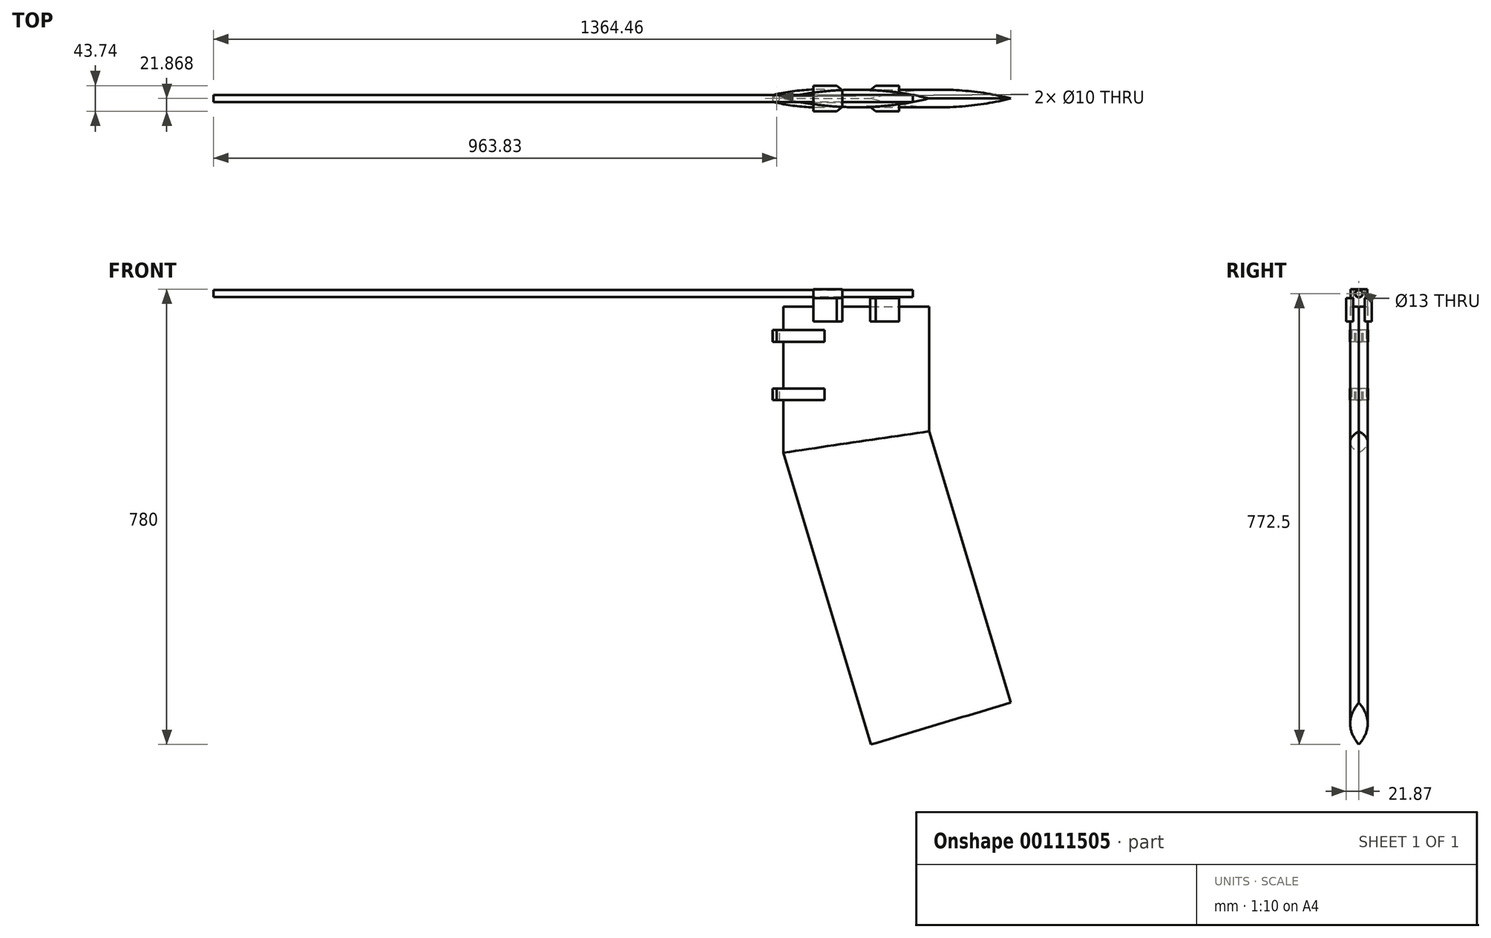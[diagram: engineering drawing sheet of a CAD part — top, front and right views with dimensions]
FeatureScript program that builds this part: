
annotation { "Feature Type Name" : "Feature", "Feature Type Description" : "" }
export const myFeature = defineFeature(function(context is Context, id is Id, definition is map)
    precondition{}
    {
        {
            var Q0;
            Q0=qCreatedBy(makeId("Front.planeOp"),FACE);
            var sketch = newSketch(context, id + "F0", { "sketchPlane" : qUnion([Q0])});
            skLineSegment(sketch, "E0.bottom", {"start": v(-150, 364.56) * mm, "end": v(100, 364.56) * mm});
            skLineSegment(sketch, "E0.top", {"start": v(0, -385.44) * mm, "end": v(250, -385.44) * mm});
            skLineSegment(sketch, "E0.left", {"start": v(-150, 364.56) * mm, "end": v(-150, 114.56) * mm});
            skLineSegment(sketch, "E1", {"start": v(100, 364.56) * mm, "end": v(100, 264.56) * mm});
            skArc(sketch, "E2", {"start": v(250, -385.44) * mm, "mid": v(188.28, -57.37) * mm, "end": v(100, 264.56) * mm});
            skLineSegment(sketch, "E3", {"start": v(250, -385.44) * mm, "end": v(0, -385.44) * mm});
            skLineSegment(sketch, "E4", {"start": v(-150, 114.56) * mm, "end": v(0, -385.44) * mm});
            skSolve(sketch);
        }
        {
            var Q0;
            Q0=sQuery(id+"F0.wireOp",EDGE,"E0.bottom");
            cPlane(context, id + "F1", {"entities" : qUnion([Q0]), "cplaneType" : CPlaneType.LINE_ANGLE, "offset" : 150 * mm, "angle" : 90 * degree, "width" : 150 * mm, "height" : 150 * mm});
        }
        {
            var Q0;
            Q0=qCreatedBy(id+"F1.planeOp",FACE);
            var sketch = newSketch(context, id + "F2", { "sketchPlane" : qUnion([Q0])});
            skLineSegment(sketch, "E5", {"start": v(-150, 0) * mm, "end": v(100, 0) * mm});
            skArc(sketch, "E6", {"start": v(100, 0) * mm, "mid": v(-25, 15) * mm, "end": v(-150, 0) * mm});
            skArc(sketch, "E7.MirrorCS", {"start": v(100, 0) * mm, "mid": v(-25, -15) * mm, "end": v(-150, 0) * mm});
            skSolve(sketch);
        }
        {
            var Q0;
            Q0=makeQuery(id+"F2.imprint","IMPRINT",FACE,{"disambiguationData":[TD([[makeQuery(id+"F2.imprint","IMPRINT",EDGE,{"derivedFrom":sQuery(id+"F2.wireOp",EDGE,"E5")}),1.0]])]});
            var Q1;
            Q1=makeQuery(id+"F2.imprint","IMPRINT",FACE,{"disambiguationData":[TD([[makeQuery(id+"F2.imprint","IMPRINT",EDGE,{"derivedFrom":sQuery(id+"F2.wireOp",EDGE,"E5")}),-1.0]])]});
            var Q2;
            Q2=sQuery(id+"F0.wireOp",EDGE,"E0.left");
            var Q3;
            Q3=sQuery(id+"F0.wireOp",EDGE,"E4");
            sweep(context, id + "F3", {"profiles" : qUnion([Q0, Q1]), "path" : qUnion([Q2, Q3])});
        }
        {
            var Q0;
            Q0=qCreatedBy(id+"F1.planeOp",FACE);
            var sketch = newSketch(context, id + "F4", { "sketchPlane" : qUnion([Q0])});
            skArc(sketch, "E8", {"start": v(-150, 0) * mm, "mid": v(-25, -15) * mm, "end": v(100, 0) * mm, "construction": true});
            skArc(sketch, "E9", {"start": v(100, 0) * mm, "mid": v(-25, 15) * mm, "end": v(-150, 0) * mm, "construction": true});
            skPoint(sketch, "E10", {"position": v(-79.2, 12.21) * mm});
            skArc(sketch, "E11", {"start": v(-161.17, 7.32) * mm, "mid": v(-168.49, 0) * mm, "end": v(-161.17, -7.32) * mm});
            skPoint(sketch, "E12", {"position": v(-161.17, 7.32) * mm});
            skArc(sketch, "E13", {"start": v(-161.17, -7.32) * mm, "mid": v(-120.44, -13.9) * mm, "end": v(-79.2, -15.21) * mm});
            skPoint(sketch, "E14.start.orphan", {"position": v(-79.2, 0) * mm});
            skCircle(sketch, "E15", {"center": v(-161.17, 0) * mm, "radius": 5 * mm});
            skLineSegment(sketch, "E16", {"start": v(-161.17, 0) * mm, "end": v(-150, 0) * mm});
            skArc(sketch, "E17.MirrorCS", {"start": v(-161.17, 7.32) * mm, "mid": v(-120.44, 13.9) * mm, "end": v(-79.2, 15.23) * mm});
            skPoint(sketch, "E18.start.orphan", {"position": v(-79.2, -12.21) * mm});
            skLineSegment(sketch, "E19", {"start": v(-79.2, 15.23) * mm, "end": v(-79.2, -15.21) * mm});
            skSolve(sketch);
        }
        {
            var Q0;
            {var subQ1=sQuery(id+"F4.wireOp",EDGE,"E13");Q0=makeQuery(id+"F4.imprint","IMPRINT",FACE,{"disambiguationData":[TD([[makeQuery(id+"F4.imprint","IMPRINT",EDGE,{"derivedFrom":subQ1}),1.0]])]});}
            extrude(context, id + "F5", {"entities" : qUnion([Q0]), "operationType" : NewBodyOperationType.ADD, "oppositeDirection" : true, "depth" : 60 * mm, "hasSecondDirection" : true, "secondDirectionOppositeDirection" : true, "secondDirectionDepth" : 40 * mm});
        }
        {
            var Q0;
            Q0=qSketchRegion(id+"F4",true);
            extrude(context, id + "F6", {"entities" : qUnion([Q0]), "operationType" : NewBodyOperationType.ADD, "oppositeDirection" : true, "depth" : 160 * mm, "hasSecondDirection" : true, "secondDirectionOppositeDirection" : true, "secondDirectionDepth" : 140 * mm});
        }
        {
            var Q0;
            Q0=qCreatedBy(id+"F1.planeOp",FACE);
            var sketch = newSketch(context, id + "F7", { "sketchPlane" : qUnion([Q0])});
            skArc(sketch, "E20.0", {"start": v(-150, 0) * mm, "mid": v(-25, -15) * mm, "end": v(100, 0) * mm});
            skArc(sketch, "E21.0", {"start": v(100, 0) * mm, "mid": v(-25, 15) * mm, "end": v(-150, 0) * mm});
            skLineSegment(sketch, "E22", {"start": v(-150, 0) * mm, "end": v(100, 0) * mm});
            skLineSegment(sketch, "E23", {"start": v(-98.48, -9.87) * mm, "end": v(-98.48, 9.87) * mm});
            skLineSegment(sketch, "E24", {"start": v(-98.48, 21.87) * mm, "end": v(-98.48, 9.87) * mm});
            skLineSegment(sketch, "E25", {"start": v(-98.48, 21.87) * mm, "end": v(-58.48, 21.87) * mm});
            skPoint(sketch, "E26.start.orphan", {"position": v(-58.48, 13.94) * mm});
            skLineSegment(sketch, "E27", {"start": v(-58.48, 21.87) * mm, "end": v(-49.05, 14.45) * mm});
            skLineSegment(sketch, "E28.MirrorCS", {"start": v(-98.48, -21.87) * mm, "end": v(-58.48, -21.87) * mm});
            skLineSegment(sketch, "E29.MirrorCS", {"start": v(-58.48, -21.87) * mm, "end": v(-49.05, -14.45) * mm});
            skLineSegment(sketch, "E30.MirrorCS", {"start": v(-98.48, -21.87) * mm, "end": v(-98.48, -9.87) * mm});
            skLineSegment(sketch, "E31", {"start": v(-49.05, -14.45) * mm, "end": v(-49.05, 14.45) * mm});
            skLineSegment(sketch, "E32", {"start": v(100, 0) * mm, "end": v(-0.96, 0) * mm});
            skPoint(sketch, "E33", {"position": v(-25, 0) * mm});
            skLineSegment(sketch, "E34", {"start": v(-25, -15) * mm, "end": v(-25, 15) * mm});
            skLineSegment(sketch, "E35.MirrorCS", {"start": v(-0.95, -14.45) * mm, "end": v(-0.95, 14.45) * mm});
            skLineSegment(sketch, "E36.MirrorCS", {"start": v(8.48, -21.87) * mm, "end": v(-0.95, -14.45) * mm});
            skLineSegment(sketch, "E37.MirrorCS", {"start": v(48.48, -21.87) * mm, "end": v(8.48, -21.87) * mm});
            skLineSegment(sketch, "E38.MirrorCS", {"start": v(48.48, -21.87) * mm, "end": v(48.48, -9.87) * mm});
            skLineSegment(sketch, "E39.MirrorCS", {"start": v(48.48, -9.87) * mm, "end": v(48.48, 9.87) * mm});
            skLineSegment(sketch, "E40.MirrorCS", {"start": v(48.48, 21.87) * mm, "end": v(48.48, 9.87) * mm});
            skLineSegment(sketch, "E41.MirrorCS", {"start": v(48.48, 21.87) * mm, "end": v(8.48, 21.87) * mm});
            skLineSegment(sketch, "E42.MirrorCS", {"start": v(8.48, 21.87) * mm, "end": v(-0.95, 14.45) * mm});
            skSolve(sketch);
        }
        {
            var Q0;
            Q0=makeQuery(id+"F7.imprint","IMPRINT",FACE,{"disambiguationData":[TD([[makeQuery(id+"F7.imprint","IMPRINT",EDGE,{"derivedFrom":sQuery(id+"F7.wireOp",EDGE,"E28.MirrorCS")}),1.0]])]});
            var Q1;
            {var subQ0=sQuery(id+"F7.wireOp",EDGE,"E36.MirrorCS");Q1=makeQuery(id+"F7.imprint","IMPRINT",FACE,{"disambiguationData":[TD([[makeQuery(id+"F7.imprint","IMPRINT",EDGE,{"derivedFrom":subQ0}),-1.0]])]});}
            var Q2;
            {var subQ0=sQuery(id+"F7.wireOp",EDGE,"E24");Q2=makeQuery(id+"F7.imprint","IMPRINT",FACE,{"disambiguationData":[TD([[makeQuery(id+"F7.imprint","IMPRINT",EDGE,{"derivedFrom":subQ0}),1.0]])]});}
            var Q3;
            {var subQ2=sQuery(id+"F7.wireOp",EDGE,"E40.MirrorCS");Q3=makeQuery(id+"F7.imprint","IMPRINT",FACE,{"disambiguationData":[TD([[makeQuery(id+"F7.imprint","IMPRINT",EDGE,{"derivedFrom":subQ2}),-1.0]])]});}
            extrude(context, id + "F8", {"entities" : qUnion([Q0, Q1, Q2, Q3]), "operationType" : NewBodyOperationType.ADD, "depth" : 15 * mm, "hasSecondDirection" : true, "secondDirectionOppositeDirection" : true, "secondDirectionDepth" : 25 * mm});
        }
        {
            var Q0;
            {var subQ3=sQuery(id+"F7.wireOp",EDGE,"E39.MirrorCS");var subQ5=sQuery(id+"F7.wireOp",EDGE,"E32");var subQ7=makeQuery(id+"F7.imprint","INTERSECT",VERTEX,{"derivedFrom":[subQ5,subQ3]});Q0=makeQuery(id+"F7.imprint","IMPRINT",FACE,{"disambiguationData":[TD([[makeQuery(id+"F7.imprint","IMPRINT",EDGE,{"disambiguationData":[TD([[subQ7,-1.0]])],"derivedFrom":subQ5}),-1.0]])]});}
            var Q1;
            {var subQ3=sQuery(id+"F7.wireOp",EDGE,"E39.MirrorCS");var subQ5=sQuery(id+"F7.wireOp",EDGE,"E32");var subQ7=makeQuery(id+"F7.imprint","INTERSECT",VERTEX,{"derivedFrom":[subQ5,subQ3]});Q1=makeQuery(id+"F7.imprint","IMPRINT",FACE,{"disambiguationData":[TD([[makeQuery(id+"F7.imprint","IMPRINT",EDGE,{"disambiguationData":[TD([[subQ7,-1.0]])],"derivedFrom":subQ5}),1.0]])]});}
            var Q2;
            {var subQ0=sQuery(id+"F7.wireOp",EDGE,"E23");var subQ5=sQuery(id+"F7.wireOp",EDGE,"E22");var subQ6=makeQuery(id+"F7.imprint","INTERSECT",VERTEX,{"derivedFrom":[subQ5,subQ0]});Q2=makeQuery(id+"F7.imprint","IMPRINT",FACE,{"disambiguationData":[TD([[makeQuery(id+"F7.imprint","IMPRINT",EDGE,{"disambiguationData":[TD([[subQ6,-1.0]])],"derivedFrom":subQ5}),-1.0]])]});}
            var Q3;
            {var subQ0=sQuery(id+"F7.wireOp",EDGE,"E23");var subQ5=sQuery(id+"F7.wireOp",EDGE,"E22");var subQ6=makeQuery(id+"F7.imprint","INTERSECT",VERTEX,{"derivedFrom":[subQ5,subQ0]});Q3=makeQuery(id+"F7.imprint","IMPRINT",FACE,{"disambiguationData":[TD([[makeQuery(id+"F7.imprint","IMPRINT",EDGE,{"disambiguationData":[TD([[subQ6,-1.0]])],"derivedFrom":subQ5}),1.0]])]});}
            extrude(context, id + "F9", {"entities" : qUnion([Q0, Q1, Q2, Q3]), "operationType" : NewBodyOperationType.ADD, "depth" : 30 * mm});
        }
        {
            var Q0;
            Q0=qCreatedBy(makeId("Right.planeOp"),FACE);
            var sketch = newSketch(context, id + "F10", { "sketchPlane" : qUnion([Q0])});
            skLineSegment(sketch, "E43.0", {"start": v(-9.87, 394.56) * mm, "end": v(9.87, 394.56) * mm});
            skLineSegment(sketch, "E44.0.0", {"start": v(-21.87, 339.56) * mm, "end": v(-9.87, 339.56) * mm});
            skLineSegment(sketch, "E44.0.1", {"start": v(-9.87, 339.56) * mm, "end": v(-9.87, 364.56) * mm});
            skLineSegment(sketch, "E44.0.2", {"start": v(-9.87, 364.56) * mm, "end": v(9.87, 364.56) * mm});
            skLineSegment(sketch, "E44.0.3", {"start": v(9.87, 364.56) * mm, "end": v(9.87, 339.56) * mm});
            skLineSegment(sketch, "E44.0.4", {"start": v(9.87, 339.56) * mm, "end": v(21.87, 339.56) * mm});
            skLineSegment(sketch, "E44.0.5", {"start": v(21.87, 339.56) * mm, "end": v(21.87, 379.56) * mm});
            skLineSegment(sketch, "E44.0.6", {"start": v(21.87, 379.56) * mm, "end": v(9.87, 379.56) * mm});
            skLineSegment(sketch, "E44.0.7", {"start": v(9.87, 379.56) * mm, "end": v(9.87, 394.56) * mm});
            skLineSegment(sketch, "E44.0.8", {"start": v(9.87, 394.56) * mm, "end": v(-9.87, 394.56) * mm});
            skLineSegment(sketch, "E44.0.9", {"start": v(-9.87, 394.56) * mm, "end": v(-9.87, 379.56) * mm});
            skLineSegment(sketch, "E44.0.10", {"start": v(-9.87, 379.56) * mm, "end": v(-21.87, 379.56) * mm});
            skLineSegment(sketch, "E44.0.11", {"start": v(-21.87, 379.56) * mm, "end": v(-21.87, 339.56) * mm});
            skLineSegment(sketch, "E45", {"start": v(9.87, 394.56) * mm, "end": v(-9.87, 379.56) * mm});
            skLineSegment(sketch, "E46", {"start": v(-9.87, 394.56) * mm, "end": v(9.87, 379.56) * mm});
            skCircle(sketch, "E47", {"center": v(0, 387.06) * mm, "radius": 7.5 * mm});
            skSolve(sketch);
        }
        {
            var Q0;
            Q0=sQuery(id+"F10.wireOp",VERTEX,"E47.center");
            var Q1;
            Q1=makeQuery(id+"F3.opSweep","SWEPT_BODY",BODY,{"disambiguationData":[OSD([sQuery(id+"F0.wireOp",EDGE,"E4"),sQuery(id+"F2.wireOp",EDGE,"E6"),sQuery(id+"F2.wireOp",EDGE,"E7.MirrorCS")])]});
            hole(context, id + "F11", {"style" : HoleStyle.SIMPLE, "holeDiameter" : 13 * mm, "endStyle" : HoleEndStyle.THROUGH, "locations" : qUnion([Q0]), "scope" : qUnion([Q1])});
        }
        {
            var Q0;
            Q0=sQuery(id+"F10.wireOp",VERTEX,"E47.center");
            var Q1;
            Q1=makeQuery(id+"F3.opSweep","SWEPT_BODY",BODY,{"disambiguationData":[OSD([sQuery(id+"F0.wireOp",EDGE,"E4"),sQuery(id+"F2.wireOp",EDGE,"E6"),sQuery(id+"F2.wireOp",EDGE,"E7.MirrorCS")])]});
            hole(context, id + "F12", {"style" : HoleStyle.SIMPLE, "holeDiameter" : 13 * mm, "endStyle" : HoleEndStyle.THROUGH, "oppositeDirection" : true, "locations" : qUnion([Q0]), "scope" : qUnion([Q1])});
        }
        {
            var Q0;
            Q0=qCreatedBy(makeId("Right.planeOp"),FACE);
            var sketch = newSketch(context, id + "F13", { "sketchPlane" : qUnion([Q0])});
            skCircle(sketch, "E48.0", {"center": v(0, 387.06) * mm, "radius": 6.5 * mm});
            skCircle(sketch, "E49", {"center": v(0, 387.06) * mm, "radius": 6 * mm});
            skSolve(sketch);
        }
        {
            var Q0;
            Q0=makeQuery(id+"F13.imprint","IMPRINT",FACE,{"disambiguationData":[TD([[makeQuery(id+"F13.imprint","IMPRINT",EDGE,{"derivedFrom":sQuery(id+"F13.wireOp",EDGE,"E49")}),1.0]])]});
            extrude(context, id + "F14", {"entities" : qUnion([Q0]), "depth" : 72 * mm, "hasSecondDirection" : true, "secondDirectionOppositeDirection" : true, "secondDirectionDepth" : 1125 * mm});
        }
    });
